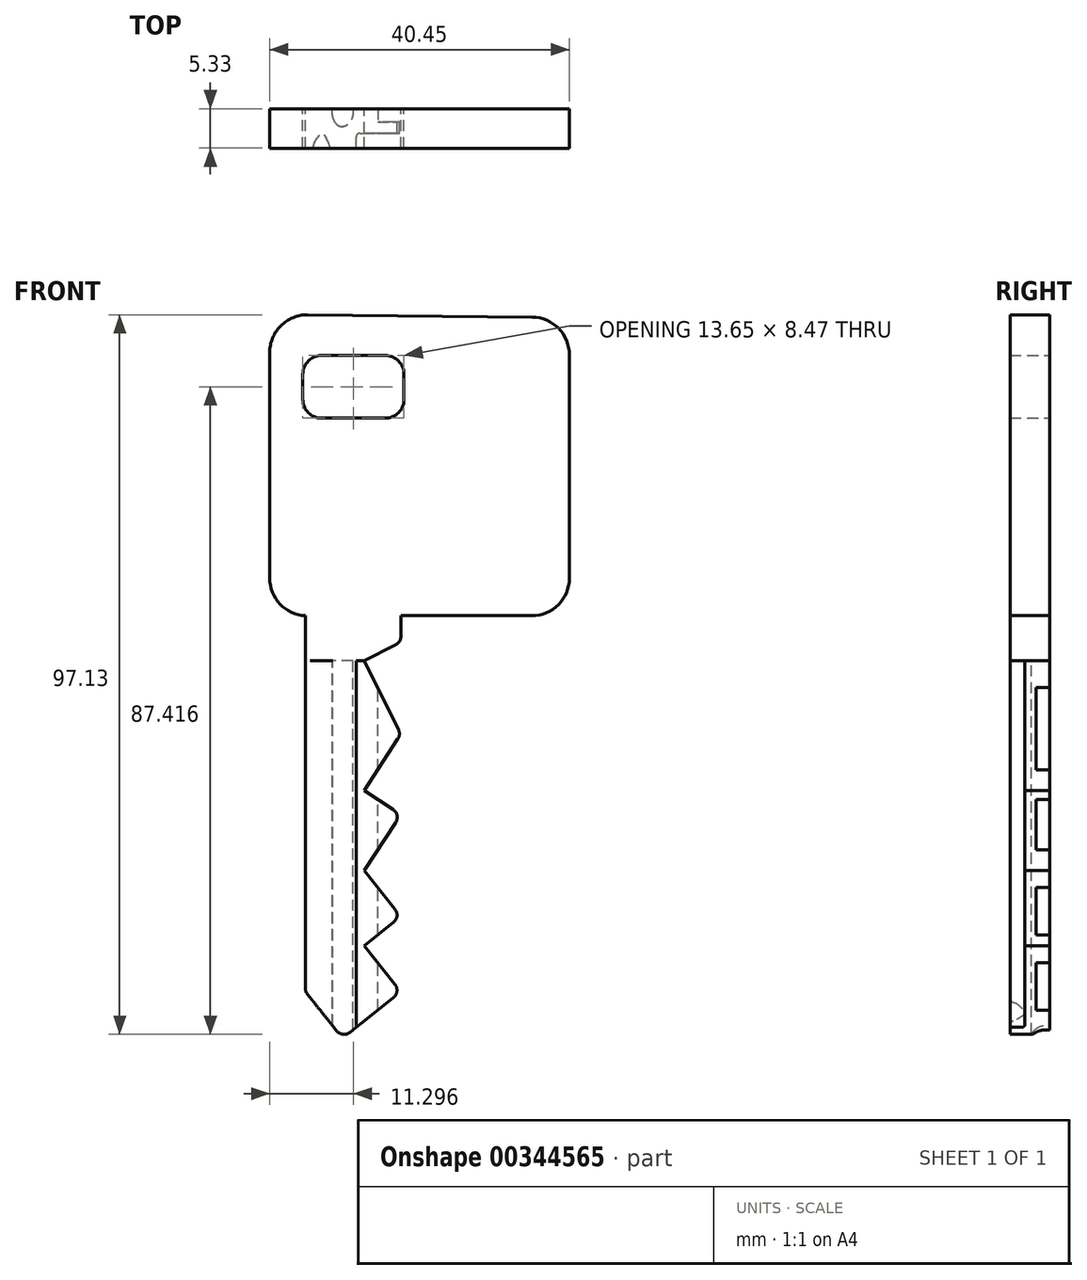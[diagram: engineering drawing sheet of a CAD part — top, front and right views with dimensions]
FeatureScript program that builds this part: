
annotation { "Feature Type Name" : "Feature", "Feature Type Description" : "" }
export const myFeature = defineFeature(function(context is Context, id is Id, definition is map)
    precondition{}
    {
        {
            var Q0;
            Q0=qCreatedBy(makeId("Front.planeOp"),FACE);
            var sketch = newSketch(context, id + "F0", { "sketchPlane" : qUnion([Q0])});
            skLineSegment(sketch, "E0", {"start": v(0, 46.72) * mm, "end": v(0, 6.04) * mm});
            skLineSegment(sketch, "E1", {"start": v(0, 6.04) * mm, "end": v(4.8, 6.04) * mm});
            skLineSegment(sketch, "E2", {"start": v(4.8, 6.04) * mm, "end": v(4.8, -44.7) * mm});
            skLineSegment(sketch, "E3", {"start": v(4.8, -44.7) * mm, "end": v(9.84, -50.98) * mm});
            skLineSegment(sketch, "E4", {"start": v(9.84, -50.98) * mm, "end": v(17.7, -44.7) * mm});
            skLineSegment(sketch, "E5", {"start": v(17.7, -44.7) * mm, "end": v(12.75, -38.5) * mm});
            skLineSegment(sketch, "E6", {"start": v(12.75, -38.5) * mm, "end": v(17.7, -34.54) * mm});
            skLineSegment(sketch, "E7", {"start": v(17.7, -34.54) * mm, "end": v(12.75, -28.36) * mm});
            skLineSegment(sketch, "E8", {"start": v(12.75, -28.36) * mm, "end": v(17.7, -20.8) * mm});
            skLineSegment(sketch, "E9", {"start": v(17.7, -20.8) * mm, "end": v(12.75, -17.55) * mm});
            skLineSegment(sketch, "E10", {"start": v(12.75, -17.55) * mm, "end": v(17.7, -9.99) * mm});
            skLineSegment(sketch, "E11", {"start": v(17.7, -9.99) * mm, "end": v(12.75, 0) * mm});
            skLineSegment(sketch, "E12", {"start": v(12.75, 0) * mm, "end": v(17.7, 2.45) * mm});
            skLineSegment(sketch, "E13", {"start": v(17.7, 2.45) * mm, "end": v(17.7, 6.04) * mm});
            skLineSegment(sketch, "E14", {"start": v(17.7, 6.04) * mm, "end": v(40.45, 6.04) * mm});
            skLineSegment(sketch, "E15", {"start": v(40.45, 6.04) * mm, "end": v(40.45, 46.3) * mm});
            skLineSegment(sketch, "E16", {"start": v(40.45, 46.3) * mm, "end": v(0, 46.72) * mm});
            skLineSegment(sketch, "E17.bottom", {"start": v(4.47, 41.18) * mm, "end": v(18.12, 41.18) * mm});
            skLineSegment(sketch, "E17.top", {"start": v(4.47, 32.7) * mm, "end": v(18.12, 32.7) * mm});
            skLineSegment(sketch, "E17.left", {"start": v(4.47, 41.18) * mm, "end": v(4.47, 32.7) * mm});
            skLineSegment(sketch, "E17.right", {"start": v(18.12, 41.18) * mm, "end": v(18.12, 32.7) * mm});
            skSolve(sketch);
        }
        {
            var Q0;
            Q0=makeQuery(id+"F0.imprint","IMPRINT",FACE,{"disambiguationData":[TD([[makeQuery(id+"F0.imprint","IMPRINT",EDGE,{"derivedFrom":sQuery(id+"F0.wireOp",EDGE,"E0")}),1.0]])]});
            extrude(context, id + "F1", {"entities" : qUnion([Q0]), "depth" : 5.33 * mm});
        }
        {
            var Q0;
            Q0=makeQuery(id+"F1.opExtrude","SWEPT_EDGE",EDGE,{"disambiguationData":[OSD([sQuery(id+"F0.wireOp",EDGE,"E14"),sQuery(id+"F0.wireOp",EDGE,"E15")])]});
            var Q1;
            Q1=makeQuery(id+"F1.opExtrude","SWEPT_EDGE",EDGE,{"disambiguationData":[OSD([sQuery(id+"F0.wireOp",EDGE,"E0"),sQuery(id+"F0.wireOp",EDGE,"E16")])]});
            var Q2;
            Q2=makeQuery(id+"F1.opExtrude","SWEPT_EDGE",EDGE,{"disambiguationData":[OSD([sQuery(id+"F0.wireOp",EDGE,"E0"),sQuery(id+"F0.wireOp",EDGE,"E1")])]});
            var Q3;
            Q3=makeQuery(id+"F1.opExtrude","SWEPT_EDGE",EDGE,{"disambiguationData":[OSD([sQuery(id+"F0.wireOp",EDGE,"E15"),sQuery(id+"F0.wireOp",EDGE,"E16")])]});
            fillet(context, id + "F2", {"entities" : qUnion([Q0, Q1, Q2, Q3]), "radius" : 5.08 * mm, "tangentPropagation" : true, "allowEdgeOverflow" : false});
        }
        {
            var Q0;
            Q0=makeQuery(id+"F1.opExtrude","SWEPT_EDGE",EDGE,{"disambiguationData":[OSD([sQuery(id+"F0.wireOp",EDGE,"E17.bottom"),sQuery(id+"F0.wireOp",EDGE,"E17.right")])]});
            var Q1;
            Q1=makeQuery(id+"F1.opExtrude","SWEPT_EDGE",EDGE,{"disambiguationData":[OSD([sQuery(id+"F0.wireOp",EDGE,"E17.bottom"),sQuery(id+"F0.wireOp",EDGE,"E17.left")])]});
            var Q2;
            Q2=makeQuery(id+"F1.opExtrude","SWEPT_EDGE",EDGE,{"disambiguationData":[OSD([sQuery(id+"F0.wireOp",EDGE,"E17.top"),sQuery(id+"F0.wireOp",EDGE,"E17.left")])]});
            var Q3;
            Q3=makeQuery(id+"F1.opExtrude","SWEPT_EDGE",EDGE,{"disambiguationData":[OSD([sQuery(id+"F0.wireOp",EDGE,"E17.top"),sQuery(id+"F0.wireOp",EDGE,"E17.right")])]});
            fillet(context, id + "F3", {"entities" : qUnion([Q0, Q1, Q2, Q3]), "radius" : 2.54 * mm, "tangentPropagation" : true, "allowEdgeOverflow" : false});
        }
        {
            var Q0;
            Q0=makeQuery(id+"F1.opExtrude","SWEPT_EDGE",EDGE,{"disambiguationData":[OSD([sQuery(id+"F0.wireOp",EDGE,"E12"),sQuery(id+"F0.wireOp",EDGE,"E13")])]});
            var Q1;
            Q1=makeQuery(id+"F1.opExtrude","SWEPT_EDGE",EDGE,{"disambiguationData":[OSD([sQuery(id+"F0.wireOp",EDGE,"E10"),sQuery(id+"F0.wireOp",EDGE,"E11")])]});
            var Q2;
            Q2=makeQuery(id+"F1.opExtrude","SWEPT_EDGE",EDGE,{"disambiguationData":[OSD([sQuery(id+"F0.wireOp",EDGE,"E8"),sQuery(id+"F0.wireOp",EDGE,"E9")])]});
            var Q3;
            Q3=makeQuery(id+"F1.opExtrude","SWEPT_EDGE",EDGE,{"disambiguationData":[OSD([sQuery(id+"F0.wireOp",EDGE,"E6"),sQuery(id+"F0.wireOp",EDGE,"E7")])]});
            var Q4;
            Q4=makeQuery(id+"F1.opExtrude","SWEPT_EDGE",EDGE,{"disambiguationData":[OSD([sQuery(id+"F0.wireOp",EDGE,"E4"),sQuery(id+"F0.wireOp",EDGE,"E5")])]});
            var Q5;
            Q5=makeQuery(id+"F1.opExtrude","SWEPT_EDGE",EDGE,{"disambiguationData":[OSD([sQuery(id+"F0.wireOp",EDGE,"E3"),sQuery(id+"F0.wireOp",EDGE,"E4")])]});
            var Q6;
            Q6=makeQuery(id+"F1.opExtrude","SWEPT_EDGE",EDGE,{"disambiguationData":[OSD([sQuery(id+"F0.wireOp",EDGE,"E2"),sQuery(id+"F0.wireOp",EDGE,"E3")])]});
            fillet(context, id + "F4", {"entities" : qUnion([Q0, Q1, Q2, Q3, Q4, Q5, Q6]), "radius" : 1.27 * mm, "tangentPropagation" : true, "allowEdgeOverflow" : false});
        }
        {
            var Q0;
            Q0=qCreatedBy(makeId("Top.planeOp"),FACE);
            var sketch = newSketch(context, id + "F5", { "sketchPlane" : qUnion([Q0])});
            skLineSegment(sketch, "E18.bottom", {"start": v(6, -5.36) * mm, "end": v(8.02, -5.36) * mm});
            skFitSpline(sketch, "E19", {"points": [v(6, -5.36) * mm, v(6, -4.72) * mm, v(6.35, -4.08) * mm, v(6.88, -3.41) * mm, v(7.19, -3.36) * mm, v(7.66, -4.1) * mm, v(7.96, -4.77) * mm, v(8.02, -5.36) * mm], "startDerivative": vector(-0.56, 4.7) * mm, "endDerivative": vector(0.01, -4.44) * mm});
            skSolve(sketch);
        }
        {
            var Q0;
            Q0 = qSketchRegion(id + "F5", true);
            extrude(context, id + "F6", {"entities" : qUnion([Q0]), "operationType" : NewBodyOperationType.REMOVE, "oppositeDirection" : true, "depth" : 52.15 * mm});
        }
        {
            var Q0;
            Q0=qCreatedBy(makeId("Top.planeOp"),FACE);
            var sketch = newSketch(context, id + "F7", { "sketchPlane" : qUnion([Q0])});
            skLineSegment(sketch, "E20.bottom", {"start": v(11.67, -5.36) * mm, "end": v(18.14, -5.36) * mm});
            skLineSegment(sketch, "E20.top", {"start": v(11.67, -3.31) * mm, "end": v(18.14, -3.31) * mm});
            skLineSegment(sketch, "E20.left", {"start": v(11.67, -5.36) * mm, "end": v(11.67, -3.31) * mm});
            skLineSegment(sketch, "E20.right", {"start": v(18.14, -5.36) * mm, "end": v(18.14, -3.31) * mm});
            skSolve(sketch);
        }
        {
            var Q0;
            Q0 = qSketchRegion(id + "F7", true);
            extrude(context, id + "F8", {"entities" : qUnion([Q0]), "operationType" : NewBodyOperationType.REMOVE, "oppositeDirection" : true, "depth" : 58.93 * mm});
        }
        {
            var Q0;
            Q0=qCreatedBy(makeId("Top.planeOp"),FACE);
            var sketch = newSketch(context, id + "F9", { "sketchPlane" : qUnion([Q0])});
            skLineSegment(sketch, "E21.bottom", {"start": v(17.63, 0) * mm, "end": v(14.57, 0) * mm});
            skLineSegment(sketch, "E21.top", {"start": v(17.63, -1.84) * mm, "end": v(14.57, -1.84) * mm});
            skLineSegment(sketch, "E21.left", {"start": v(17.63, 0) * mm, "end": v(17.63, -1.84) * mm});
            skLineSegment(sketch, "E21.right", {"start": v(14.57, 0) * mm, "end": v(14.57, -1.84) * mm});
            skSolve(sketch);
        }
        {
            var Q0;
            Q0 = qSketchRegion(id + "F9", true);
            extrude(context, id + "F10", {"entities" : qUnion([Q0]), "operationType" : NewBodyOperationType.REMOVE, "oppositeDirection" : true, "depth" : 54.6 * mm});
        }
        {
            var Q0;
            Q0=qCreatedBy(makeId("Top.planeOp"),FACE);
            var sketch = newSketch(context, id + "F11", { "sketchPlane" : qUnion([Q0])});
            skFitSpline(sketch, "E22", {"points": [v(11.22, 0) * mm, v(11.2, -0.97) * mm, v(10.47, -2.2) * mm, v(9.22, -2.28) * mm, v(8.48, -0.86) * mm, v(8.5, 0) * mm], "startDerivative": vector(0.4, -5.13) * mm, "endDerivative": vector(0.73, 4.52) * mm});
            skLineSegment(sketch, "E23", {"start": v(11.22, 0) * mm, "end": v(8.5, 0) * mm});
            skSolve(sketch);
        }
        {
            var Q0;
            Q0 = qSketchRegion(id + "F11", true);
            extrude(context, id + "F12", {"entities" : qUnion([Q0]), "operationType" : NewBodyOperationType.REMOVE, "oppositeDirection" : true, "depth" : 55.63 * mm});
        }
        {
            var Q0;
            Q0=makeQuery(id+"F6.boolean.opBoolean","INTERSECT",EDGE,{"disambiguationData":[OD(1.0)],"derivedFrom":[makeQuery(id+"F1.opExtrude","CAP_FACE",FACE,{"disambiguationData":[OSD([sQuery(id+"F0.wireOp",EDGE,"E0"),sQuery(id+"F0.wireOp",EDGE,"E1"),sQuery(id+"F0.wireOp",EDGE,"E2"),sQuery(id+"F0.wireOp",EDGE,"E3"),sQuery(id+"F0.wireOp",EDGE,"E4"),sQuery(id+"F0.wireOp",EDGE,"E5"),sQuery(id+"F0.wireOp",EDGE,"E6"),sQuery(id+"F0.wireOp",EDGE,"E7"),sQuery(id+"F0.wireOp",EDGE,"E8"),sQuery(id+"F0.wireOp",EDGE,"E9"),sQuery(id+"F0.wireOp",EDGE,"E10"),sQuery(id+"F0.wireOp",EDGE,"E11"),sQuery(id+"F0.wireOp",EDGE,"E12"),sQuery(id+"F0.wireOp",EDGE,"E13"),sQuery(id+"F0.wireOp",EDGE,"E14"),sQuery(id+"F0.wireOp",EDGE,"E15"),sQuery(id+"F0.wireOp",EDGE,"E16"),sQuery(id+"F0.wireOp",EDGE,"E17.bottom"),sQuery(id+"F0.wireOp",EDGE,"E17.top"),sQuery(id+"F0.wireOp",EDGE,"E17.left"),sQuery(id+"F0.wireOp",EDGE,"E17.right")])],"isStart":false}),makeQuery(id+"F6.opExtrude","SWEPT_FACE",FACE,{"disambiguationData":[OSD([sQuery(id+"F5.wireOp",EDGE,"E19")])]})]});
            var Q1;
            {var subQ0=sQuery(id+"F11.wireOp",EDGE,"E23");var subQ1=sQuery(id+"F11.wireOp",EDGE,"E22");Q1=makeQuery(id+"F12.boolean.opBoolean","COPY",EDGE,{"derivedFrom":makeQuery(id+"F12.opExtrude","SWEPT_EDGE",EDGE,{"disambiguationData":[OSD([subQ1,subQ0]),TDD([makeQuery(id+"F11.imprint","INTERSECT",VERTEX,{"disambiguationData":[OD(0.0)],"derivedFrom":[subQ1,subQ0]})])]})});}
            var Q2;
            {var subQ0=sQuery(id+"F11.wireOp",EDGE,"E23");var subQ1=sQuery(id+"F11.wireOp",EDGE,"E22");Q2=makeQuery(id+"F12.boolean.opBoolean","COPY",EDGE,{"derivedFrom":makeQuery(id+"F12.opExtrude","SWEPT_EDGE",EDGE,{"disambiguationData":[OSD([subQ1,subQ0]),TDD([makeQuery(id+"F11.imprint","INTERSECT",VERTEX,{"disambiguationData":[OD(1.0)],"derivedFrom":[subQ1,subQ0]})])]})});}
            var Q3;
            Q3=makeQuery(id+"F8.boolean.opBoolean","COPY",EDGE,{"derivedFrom":makeQuery(id+"F8.opExtrude","SWEPT_EDGE",EDGE,{"disambiguationData":[OSD([sQuery(id+"F7.wireOp",EDGE,"E20.top"),sQuery(id+"F7.wireOp",EDGE,"E20.left")])]})});
            var Q4;
            Q4=makeQuery(id+"F6.boolean.opBoolean","INTERSECT",EDGE,{"disambiguationData":[OD(0.0)],"derivedFrom":[makeQuery(id+"F1.opExtrude","CAP_FACE",FACE,{"disambiguationData":[OSD([sQuery(id+"F0.wireOp",EDGE,"E0"),sQuery(id+"F0.wireOp",EDGE,"E1"),sQuery(id+"F0.wireOp",EDGE,"E2"),sQuery(id+"F0.wireOp",EDGE,"E3"),sQuery(id+"F0.wireOp",EDGE,"E4"),sQuery(id+"F0.wireOp",EDGE,"E5"),sQuery(id+"F0.wireOp",EDGE,"E6"),sQuery(id+"F0.wireOp",EDGE,"E7"),sQuery(id+"F0.wireOp",EDGE,"E8"),sQuery(id+"F0.wireOp",EDGE,"E9"),sQuery(id+"F0.wireOp",EDGE,"E10"),sQuery(id+"F0.wireOp",EDGE,"E11"),sQuery(id+"F0.wireOp",EDGE,"E12"),sQuery(id+"F0.wireOp",EDGE,"E13"),sQuery(id+"F0.wireOp",EDGE,"E14"),sQuery(id+"F0.wireOp",EDGE,"E15"),sQuery(id+"F0.wireOp",EDGE,"E16"),sQuery(id+"F0.wireOp",EDGE,"E17.bottom"),sQuery(id+"F0.wireOp",EDGE,"E17.top"),sQuery(id+"F0.wireOp",EDGE,"E17.left"),sQuery(id+"F0.wireOp",EDGE,"E17.right")])],"isStart":false}),makeQuery(id+"F6.opExtrude","SWEPT_FACE",FACE,{"disambiguationData":[OSD([sQuery(id+"F5.wireOp",EDGE,"E19")])]})]});
            fillet(context, id + "F13", {"entities" : qUnion([Q0, Q1, Q2, Q3, Q4]), "radius" : 0.5 * mm, "tangentPropagation" : true, "allowEdgeOverflow" : false});
        }
    });
